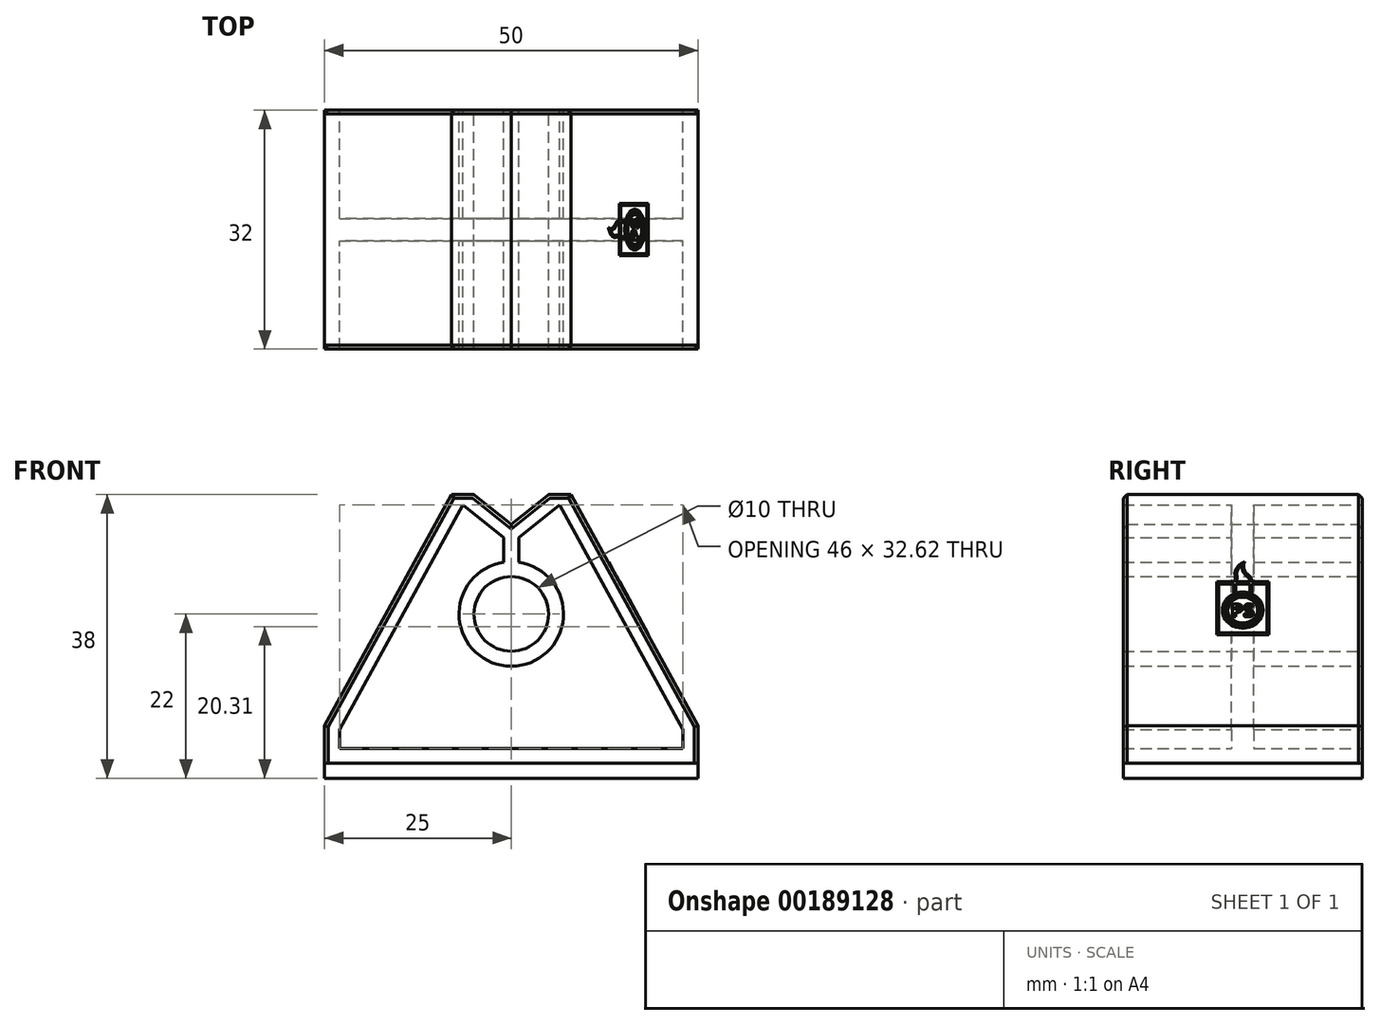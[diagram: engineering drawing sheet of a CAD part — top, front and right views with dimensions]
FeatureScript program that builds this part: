
annotation { "Feature Type Name" : "Feature", "Feature Type Description" : "" }
export const myFeature = defineFeature(function(context is Context, id is Id, definition is map)
    precondition{}
    {
        {
            var Q0;
            Q0=qCreatedBy(makeId("Front.planeOp"),FACE);
            var sketch = newSketch(context, id + "F0", { "sketchPlane" : qUnion([Q0])});
            skLineSegment(sketch, "E0", {"start": v(25, 0) * mm, "end": v(-25, 0) * mm});
            skLineSegment(sketch, "E1", {"start": v(-25, 0) * mm, "end": v(-25, 5) * mm});
            skLineSegment(sketch, "E2", {"start": v(-25, 5) * mm, "end": v(-8, 36) * mm});
            skLineSegment(sketch, "E3", {"start": v(-8, 36) * mm, "end": v(-5, 36) * mm});
            skLineSegment(sketch, "E4", {"start": v(-5, 36) * mm, "end": v(0, 32) * mm});
            skLineSegment(sketch, "E5", {"start": v(8, 36) * mm, "end": v(25, 5) * mm});
            skLineSegment(sketch, "E6", {"start": v(25, 5) * mm, "end": v(25, 0) * mm});
            skLineSegment(sketch, "E7", {"start": v(0, -2.91) * mm, "end": v(0, 50.82) * mm, "construction": true});
            skLineSegment(sketch, "E8", {"start": v(0, 32) * mm, "end": v(5, 36) * mm});
            skLineSegment(sketch, "E9", {"start": v(5, 36) * mm, "end": v(8, 36) * mm});
            skCircle(sketch, "E10", {"center": v(0, 20) * mm, "radius": 5 * mm});
            skArc(sketch, "E11.0", {"start": v(-1, 26.93) * mm, "mid": v(0, 13) * mm, "end": v(1, 26.93) * mm});
            skLineSegment(sketch, "E12.0", {"start": v(-23, 4.49) * mm, "end": v(-6.48, 34.62) * mm});
            skLineSegment(sketch, "E12.1", {"start": v(23, 2) * mm, "end": v(-23, 2) * mm});
            skLineSegment(sketch, "E12.2", {"start": v(-6.48, 34.62) * mm, "end": v(-1, 30.24) * mm});
            skLineSegment(sketch, "E12.3", {"start": v(1, 30.24) * mm, "end": v(6.48, 34.62) * mm});
            skLineSegment(sketch, "E12.4", {"start": v(6.48, 34.62) * mm, "end": v(23, 4.49) * mm});
            skLineSegment(sketch, "E13.0", {"start": v(-23, 2) * mm, "end": v(-23, 4.49) * mm});
            skLineSegment(sketch, "E14.0", {"start": v(23, 4.49) * mm, "end": v(23, 2) * mm});
            skLineSegment(sketch, "E15", {"start": v(-1, 30.24) * mm, "end": v(-1, 26.93) * mm});
            skLineSegment(sketch, "E16", {"start": v(1, 30.24) * mm, "end": v(1, 26.93) * mm});
            skSolve(sketch);
        }
        {
            var Q0;
            Q0=makeQuery(id+"F0.imprint","IMPRINT",FACE,{"disambiguationData":[TD([[makeQuery(id+"F0.imprint","IMPRINT",EDGE,{"derivedFrom":sQuery(id+"F0.wireOp",EDGE,"E0")}),-1.0]])]});
            extrude(context, id + "F1", {"entities" : qUnion([Q0]), "endBound" : BoundingType.SYMMETRIC, "depth" : 32 * mm});
        }
        {
            var Q0;
            Q0=makeQuery(id+"F0.imprint","IMPRINT",FACE,{"disambiguationData":[TD([[makeQuery(id+"F0.imprint","IMPRINT",EDGE,{"derivedFrom":sQuery(id+"F0.wireOp",EDGE,"E11.0")}),-1.0]])]});
            extrude(context, id + "F2", {"entities" : qUnion([Q0]), "operationType" : NewBodyOperationType.ADD, "endBound" : BoundingType.SYMMETRIC, "depth" : 3 * mm});
        }
        {
            var Q0;
            Q0=makeQuery(id+"F1.opExtrude","SWEPT_FACE",FACE,{"disambiguationData":[OSD([sQuery(id+"F0.wireOp",EDGE,"E0")])]});
            extrude(context, id + "F3", {"entities" : qUnion([Q0]), "depth" : 2 * mm});
        }
        {
            var Q0;
            Q0=makeQuery(id+"F1.opExtrude","SWEPT_FACE",FACE,{"disambiguationData":[OSD([sQuery(id+"F0.wireOp",EDGE,"E5")])]});
            var sketch = newSketch(context, id + "F4", { "sketchPlane" : qUnion([Q0])});
            skLineSegment(sketch, "E17.bottom", {"start": v(-3.48, 6.32) * mm, "end": v(3.48, 6.32) * mm});
            skLineSegment(sketch, "E17.top", {"start": v(-3.48, 14.32) * mm, "end": v(-1.2, 14.32) * mm});
            skLineSegment(sketch, "E17.left", {"start": v(-3.48, 6.32) * mm, "end": v(-3.48, 14.32) * mm});
            skLineSegment(sketch, "E17.right", {"start": v(3.48, 6.32) * mm, "end": v(3.48, 14.32) * mm});
            skLineSegment(sketch, "E18", {"start": v(0, 14.32) * mm, "end": v(0, 6.56) * mm, "construction": true});
            skLineSegment(sketch, "E19", {"start": v(-3.48, 10.04) * mm, "end": v(3.48, 10.04) * mm, "construction": true});
            skCircle(sketch, "E20", {"center": v(0, 10.04) * mm, "radius": 2.24 * mm});
            skCircle(sketch, "E21", {"center": v(0, 10.04) * mm, "radius": 2.48 * mm});
            skArc(sketch, "E22", {"start": v(-1.2, 12.48) * mm, "mid": v(0, 7.32) * mm, "end": v(1.2, 12.48) * mm});
            skLineSegment(sketch, "E23.bottom", {"start": v(-3.24, 6.56) * mm, "end": v(3.24, 6.56) * mm});
            skLineSegment(sketch, "E23.top", {"start": v(-3.24, 14.08) * mm, "end": v(-1.2, 14.08) * mm});
            skLineSegment(sketch, "E23.left", {"start": v(-3.24, 6.56) * mm, "end": v(-3.24, 14.08) * mm});
            skLineSegment(sketch, "E23.right", {"start": v(3.24, 6.56) * mm, "end": v(3.24, 14.08) * mm});
            skCircle(sketch, "E24", {"center": v(0, 10.04) * mm, "radius": 2 * mm});
            skText(sketch, "E25", { "text": "PS", "fontName": "OpenSans-Bold.ttf"});
            skLineSegment(sketch, "E26", {"start": v(-1.2, 14.08) * mm, "end": v(-1.2, 12.48) * mm});
            skLineSegment(sketch, "E27", {"start": v(-0.96, 14.08) * mm, "end": v(-0.96, 12.59) * mm});
            skLineSegment(sketch, "E28", {"start": v(0.96, 14.08) * mm, "end": v(0.96, 12.59) * mm});
            skLineSegment(sketch, "E29", {"start": v(1.2, 14.08) * mm, "end": v(1.2, 12.48) * mm});
            skArc(sketch, "E30.trimOffspring", {"start": v(0.96, 12.59) * mm, "mid": v(0, 12.76) * mm, "end": v(-0.96, 12.59) * mm});
            skLineSegment(sketch, "E31.trimOffspring", {"start": v(-0.96, 14.08) * mm, "end": v(0.96, 14.08) * mm});
            skLineSegment(sketch, "E32.trimOffspring", {"start": v(1.2, 14.08) * mm, "end": v(3.24, 14.08) * mm});
            skLineSegment(sketch, "E33.trimOffspring", {"start": v(-0.96, 14.32) * mm, "end": v(0.96, 14.32) * mm});
            skLineSegment(sketch, "E34.trimOffspring", {"start": v(1.2, 14.32) * mm, "end": v(3.48, 14.32) * mm});
            skFitSpline(sketch, "E35", {"points": [v(1.2, 14.32) * mm, v(0.6, 15.56) * mm, v(0.24, 17.36) * mm], "startDerivative": vector(0.25, 4.65) * mm, "endDerivative": vector(1.8, 4.26) * mm});
            skFitSpline(sketch, "E36", {"points": [v(-1.2, 14.32) * mm, v(-1.04, 15.56) * mm, v(0.24, 17.36) * mm], "startDerivative": vector(2.5, 4.2) * mm, "endDerivative": vector(5.47, 2.73) * mm});
            skFitSpline(sketch, "E37", {"points": [v(-0.96, 14.32) * mm, v(-0.8, 15.56) * mm, v(-0.06, 16.88) * mm], "startDerivative": vector(2.26, 3.78) * mm, "endDerivative": vector(2.86, 1.6) * mm});
            skFitSpline(sketch, "E38", {"points": [v(0.96, 14.32) * mm, v(0.28, 15.56) * mm, v(-0.06, 16.88) * mm], "startDerivative": vector(0.23, 4.28) * mm, "endDerivative": vector(0.6, 2.18) * mm});
            skLineSegment(sketch, "E39", {"start": v(0, -7.64) * mm, "end": v(0, 10.04) * mm, "construction": true});
            skPoint(sketch, "E39.endSnap0", {"position": v(16, 10.04) * mm});
            const initialGuessF4  = {"E25": [-0.0016, 0.00904, 1, 0, 0.00191]};
            skSetInitialGuess(sketch, initialGuessF4);
            skSolve(sketch);
        }
        {
            var Q0;
            Q0=makeQuery(id+"F4.imprint","IMPRINT",FACE,{"disambiguationData":[TD([[makeQuery(id+"F4.imprint","IMPRINT",EDGE,{"derivedFrom":sQuery(id+"F4.wireOp",EDGE,"E17.bottom")}),1.0]])]});
            var Q1;
            Q1=makeQuery(id+"F4.imprint","IMPRINT",FACE,{"disambiguationData":[TD([[makeQuery(id+"F4.imprint","IMPRINT",EDGE,{"derivedFrom":sQuery(id+"F4.wireOp",EDGE,"E20")}),1.0]])]});
            var Q2;
            Q2=makeQuery(id+"F4.imprint","IMPRINT",FACE,{"disambiguationData":[TD([[makeQuery(id+"F4.imprint","IMPRINT",EDGE,{"derivedFrom":sQuery(id+"F4.wireOp",EDGE,"E25.sketch_text.stroke-16")}),-1.0]])]});
            var Q3;
            Q3=makeQuery(id+"F4.imprint","IMPRINT",FACE,{"disambiguationData":[TD([[makeQuery(id+"F4.imprint","IMPRINT",EDGE,{"derivedFrom":sQuery(id+"F4.wireOp",EDGE,"E25.sketch_text.stroke-0")}),-1.0]])]});
            extrude(context, id + "F5", {"entities" : qUnion([Q0, Q1, Q2, Q3]), "operationType" : NewBodyOperationType.ADD, "depth" : .1 * mm});
        }
        {
            var Q0;
            Q0=makeQuery(id+"F1.opExtrude","CAP_EDGE",EDGE,{"disambiguationData":[OSD([sQuery(id+"F0.wireOp",EDGE,"E6")])],"isStart":false});
            var Q1;
            Q1=makeQuery(id+"F1.opExtrude","CAP_EDGE",EDGE,{"disambiguationData":[OSD([sQuery(id+"F0.wireOp",EDGE,"E5")])],"isStart":false});
            var Q2;
            Q2=makeQuery(id+"F1.opExtrude","CAP_EDGE",EDGE,{"disambiguationData":[OSD([sQuery(id+"F0.wireOp",EDGE,"E9")])],"isStart":false});
            var Q3;
            Q3=makeQuery(id+"F1.opExtrude","CAP_EDGE",EDGE,{"disambiguationData":[OSD([sQuery(id+"F0.wireOp",EDGE,"E8")])],"isStart":false});
            var Q4;
            Q4=makeQuery(id+"F1.opExtrude","CAP_EDGE",EDGE,{"disambiguationData":[OSD([sQuery(id+"F0.wireOp",EDGE,"E4")])],"isStart":false});
            var Q5;
            Q5=makeQuery(id+"F1.opExtrude","CAP_EDGE",EDGE,{"disambiguationData":[OSD([sQuery(id+"F0.wireOp",EDGE,"E3")])],"isStart":false});
            var Q6;
            Q6=makeQuery(id+"F1.opExtrude","CAP_EDGE",EDGE,{"disambiguationData":[OSD([sQuery(id+"F0.wireOp",EDGE,"E2")])],"isStart":false});
            var Q7;
            Q7=makeQuery(id+"F1.opExtrude","CAP_EDGE",EDGE,{"disambiguationData":[OSD([sQuery(id+"F0.wireOp",EDGE,"E1")])],"isStart":false});
            var Q8;
            Q8=makeQuery(id+"F1.opExtrude","CAP_EDGE",EDGE,{"disambiguationData":[OSD([sQuery(id+"F0.wireOp",EDGE,"E6")])],"isStart":true});
            var Q9;
            Q9=makeQuery(id+"F1.opExtrude","CAP_EDGE",EDGE,{"disambiguationData":[OSD([sQuery(id+"F0.wireOp",EDGE,"E5")])],"isStart":true});
            var Q10;
            Q10=makeQuery(id+"F1.opExtrude","CAP_EDGE",EDGE,{"disambiguationData":[OSD([sQuery(id+"F0.wireOp",EDGE,"E9")])],"isStart":true});
            var Q11;
            Q11=makeQuery(id+"F1.opExtrude","CAP_EDGE",EDGE,{"disambiguationData":[OSD([sQuery(id+"F0.wireOp",EDGE,"E8")])],"isStart":true});
            var Q12;
            Q12=makeQuery(id+"F1.opExtrude","CAP_EDGE",EDGE,{"disambiguationData":[OSD([sQuery(id+"F0.wireOp",EDGE,"E4")])],"isStart":true});
            var Q13;
            Q13=makeQuery(id+"F1.opExtrude","CAP_EDGE",EDGE,{"disambiguationData":[OSD([sQuery(id+"F0.wireOp",EDGE,"E3")])],"isStart":true});
            var Q14;
            Q14=makeQuery(id+"F1.opExtrude","CAP_EDGE",EDGE,{"disambiguationData":[OSD([sQuery(id+"F0.wireOp",EDGE,"E2")])],"isStart":true});
            var Q15;
            Q15=makeQuery(id+"F1.opExtrude","CAP_EDGE",EDGE,{"disambiguationData":[OSD([sQuery(id+"F0.wireOp",EDGE,"E1")])],"isStart":true});
            chamfer(context, id + "F6", {"entities" : qUnion([Q0, Q1, Q2, Q3, Q4, Q5, Q6, Q7, Q8, Q9, Q10, Q11, Q12, Q13, Q14, Q15]), "width" : .5 * mm, "tangentPropagation" : true});
        }
        {
            var Q0;
            Q0=makeQuery(id+"F1.opExtrude","SWEPT_EDGE",EDGE,{"disambiguationData":[OSD([sQuery(id+"F0.wireOp",EDGE,"E3"),sQuery(id+"F0.wireOp",EDGE,"E4")])]});
            var Q1;
            Q1=makeQuery(id+"F1.opExtrude","SWEPT_EDGE",EDGE,{"disambiguationData":[OSD([sQuery(id+"F0.wireOp",EDGE,"E8"),sQuery(id+"F0.wireOp",EDGE,"E9")])]});
            var Q2;
            Q2=makeQuery(id+"F6.opChamfer","BLEND_EDGE",EDGE,{"blendedFrom":[makeQuery(id+"F1.opExtrude","CAP_EDGE",EDGE,{"disambiguationData":[OSD([sQuery(id+"F0.wireOp",EDGE,"E3")])],"isStart":false}),makeQuery(id+"F1.opExtrude","CAP_EDGE",EDGE,{"disambiguationData":[OSD([sQuery(id+"F0.wireOp",EDGE,"E4")])],"isStart":false})],"blendedInto":[]});
            var Q3;
            Q3=makeQuery(id+"F6.opChamfer","BLEND_EDGE",EDGE,{"blendedFrom":[makeQuery(id+"F1.opExtrude","CAP_EDGE",EDGE,{"disambiguationData":[OSD([sQuery(id+"F0.wireOp",EDGE,"E8")])],"isStart":false}),makeQuery(id+"F1.opExtrude","CAP_EDGE",EDGE,{"disambiguationData":[OSD([sQuery(id+"F0.wireOp",EDGE,"E9")])],"isStart":false})],"blendedInto":[]});
            var Q4;
            Q4=makeQuery(id+"F6.opChamfer","BLEND_EDGE",EDGE,{"blendedFrom":[makeQuery(id+"F1.opExtrude","CAP_EDGE",EDGE,{"disambiguationData":[OSD([sQuery(id+"F0.wireOp",EDGE,"E8")])],"isStart":true}),makeQuery(id+"F1.opExtrude","CAP_EDGE",EDGE,{"disambiguationData":[OSD([sQuery(id+"F0.wireOp",EDGE,"E9")])],"isStart":true})],"blendedInto":[]});
            var Q5;
            Q5=makeQuery(id+"F6.opChamfer","BLEND_EDGE",EDGE,{"blendedFrom":[makeQuery(id+"F1.opExtrude","CAP_EDGE",EDGE,{"disambiguationData":[OSD([sQuery(id+"F0.wireOp",EDGE,"E3")])],"isStart":true}),makeQuery(id+"F1.opExtrude","CAP_EDGE",EDGE,{"disambiguationData":[OSD([sQuery(id+"F0.wireOp",EDGE,"E4")])],"isStart":true})],"blendedInto":[]});
            fillet(context, id + "F7", {"entities" : qUnion([Q0, Q1, Q2, Q3, Q4, Q5]), "radius" : .5 * mm, "tangentPropagation" : true, "allowEdgeOverflow" : false});
        }
    });
